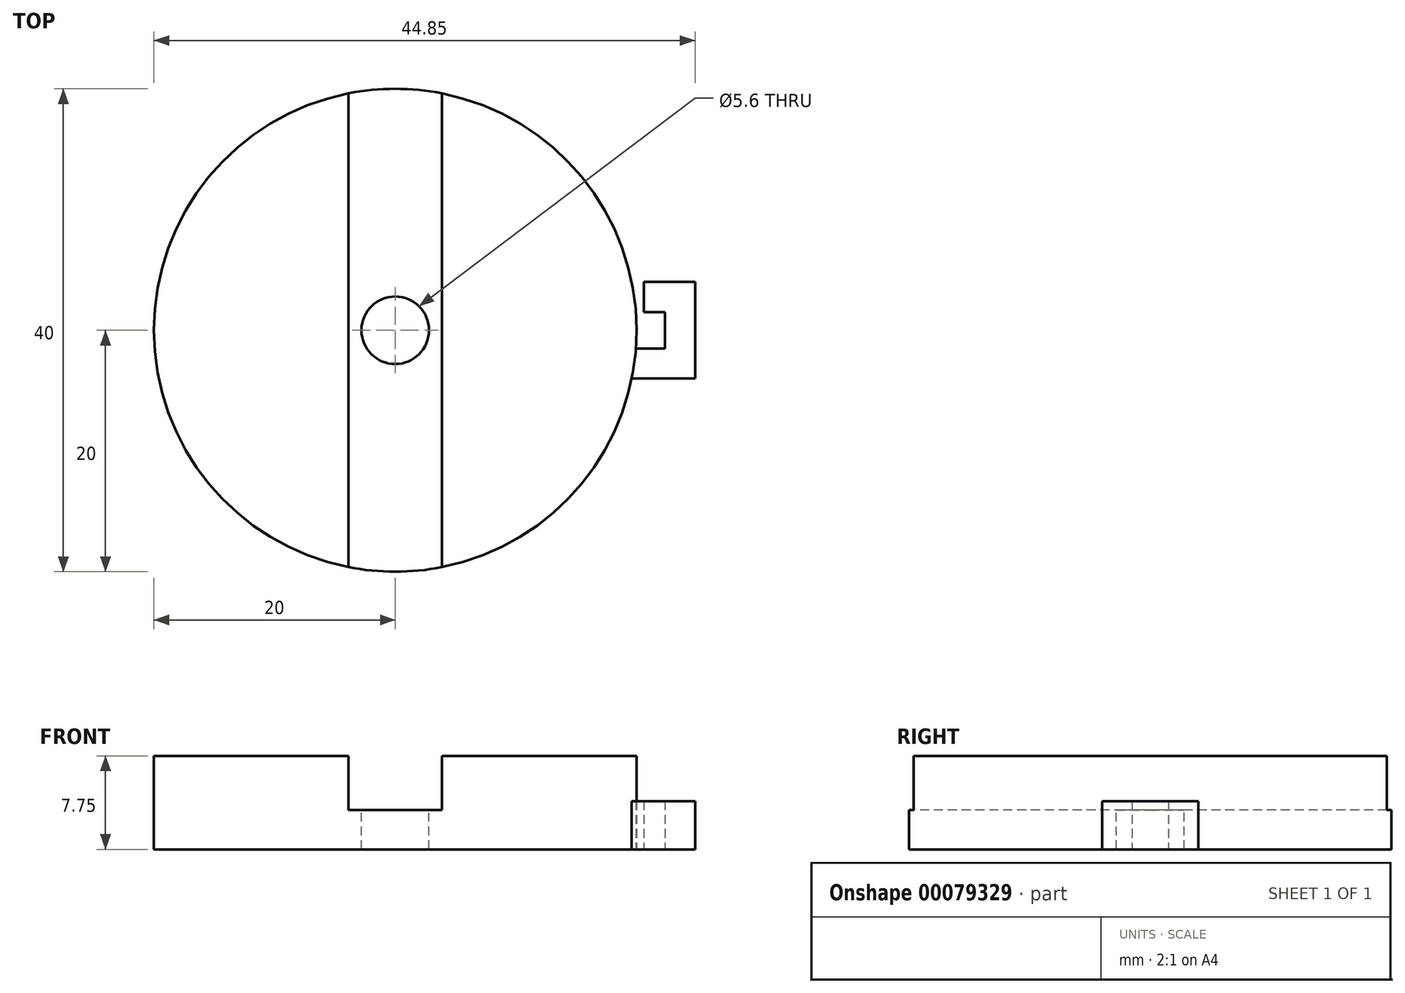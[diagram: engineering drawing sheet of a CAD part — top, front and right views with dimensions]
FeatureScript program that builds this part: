
annotation { "Feature Type Name" : "Feature", "Feature Type Description" : "" }
export const myFeature = defineFeature(function(context is Context, id is Id, definition is map)
    precondition{}
    {
        {
            var Q0;
            Q0=qCreatedBy(makeId("Top.planeOp"),FACE);
            var sketch = newSketch(context, id + "F0", { "sketchPlane" : qUnion([Q0])});
            skCircle(sketch, "E0", {"center": v(0, 0) * mm, "radius": 20 * mm});
            skSolve(sketch);
        }
        {
            var Q0;
            Q0 = qSketchRegion(id + "F0", true);
            extrude(context, id + "F1", {"entities" : qUnion([Q0]), "depth" : 7.75 * mm});
        }
        {
            var Q0;
            Q0=makeQuery(id+"F1.opExtrude","CAP_FACE",FACE,{"disambiguationData":[OSD([sQuery(id+"F0.wireOp",EDGE,"E0")])],"isStart":false});
            var sketch = newSketch(context, id + "F2", { "sketchPlane" : qUnion([Q0])});
            skLineSegment(sketch, "E1.bottom", {"start": v(3.88, 20) * mm, "end": v(-3.87, 20) * mm});
            skLineSegment(sketch, "E1.top", {"start": v(3.87, -20) * mm, "end": v(-3.88, -20) * mm});
            skLineSegment(sketch, "E1.left", {"start": v(3.88, 20) * mm, "end": v(3.87, -20) * mm});
            skLineSegment(sketch, "E1.right", {"start": v(-3.87, 20) * mm, "end": v(-3.88, -20) * mm});
            skPoint(sketch, "E1.middle", {"position": v(0, 0) * mm});
            skSolve(sketch);
        }
        {
            var Q0;
            Q0 = qSketchRegion(id + "F2", true);
            extrude(context, id + "F3", {"entities" : qUnion([Q0]), "operationType" : NewBodyOperationType.REMOVE, "oppositeDirection" : true, "depth" : 4.5 * mm});
        }
        {
            var Q0;
            Q0=qCreatedBy(makeId("Top.planeOp"),FACE);
            var sketch = newSketch(context, id + "F4", { "sketchPlane" : qUnion([Q0])});
            skLineSegment(sketch, "E2", {"start": v(18.47, -1.5) * mm, "end": v(22.35, -1.5) * mm});
            skLineSegment(sketch, "E3", {"start": v(22.35, -1.5) * mm, "end": v(22.35, 1.5) * mm});
            skLineSegment(sketch, "E4", {"start": v(22.35, 1.5) * mm, "end": v(20.6, 1.5) * mm});
            skLineSegment(sketch, "E5", {"start": v(20.6, 1.5) * mm, "end": v(20.6, 4) * mm});
            skLineSegment(sketch, "E6", {"start": v(24.85, 4) * mm, "end": v(24.85, -4) * mm});
            skLineSegment(sketch, "E7", {"start": v(24.85, -4) * mm, "end": v(19.6, -4) * mm});
            skLineSegment(sketch, "E8", {"start": v(19.6, -4) * mm, "end": v(18.47, -1.5) * mm});
            skLineSegment(sketch, "E9", {"start": v(20.6, 4) * mm, "end": v(24.85, 4) * mm});
            skSolve(sketch);
        }
        {
            var Q0;
            Q0 = qSketchRegion(id + "F4", true);
            extrude(context, id + "F5", {"entities" : qUnion([Q0]), "operationType" : NewBodyOperationType.ADD, "depth" : 4 * mm});
        }
        {
            var Q0;
            Q0=makeQuery(id+"F3.boolean.opBoolean","COPY",FACE,{"derivedFrom":makeQuery(id+"F3.opExtrude","CAP_FACE",FACE,{"disambiguationData":[OSD([sQuery(id+"F2.wireOp",EDGE,"E1.bottom"),sQuery(id+"F2.wireOp",EDGE,"E1.top"),sQuery(id+"F2.wireOp",EDGE,"E1.left"),sQuery(id+"F2.wireOp",EDGE,"E1.right")])],"isStart":false})});
            var sketch = newSketch(context, id + "F6", { "sketchPlane" : qUnion([Q0])});
            skCircle(sketch, "E10", {"center": v(0, 0) * mm, "radius": 2.8 * mm});
            skSolve(sketch);
        }
        {
            var Q0;
            Q0 = qSketchRegion(id + "F6", true);
            extrude(context, id + "F7", {"entities" : qUnion([Q0]), "operationType" : NewBodyOperationType.REMOVE, "endBound" : BoundingType.THROUGH_ALL, "oppositeDirection" : true, "depth" : 25 * mm});
        }
    });
